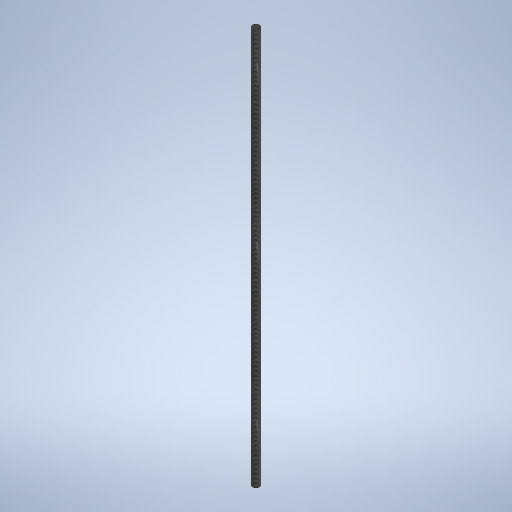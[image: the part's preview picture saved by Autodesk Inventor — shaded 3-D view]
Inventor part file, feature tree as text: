
AUTODESK INVENTOR PART (.ipt)
format: ipt  version: 2024 (Build 280153000, 153)  size: 253,440 bytes
history: native  units: mm
features: extrude x1, thread x1, sketch x1
ambient origin geometry x8: Origin, YZ Plane, XZ Plane, XY Plane, X Axis, Y Axis, Z Axis, Center Point
bodies: Solid1 (feature_tree)
feature tree (3):
  extrude  "Extrusion1"  Depth=450.0mm
  thread  "Thread1"  [1 undecoded]
  sketch  "Sketch1"  dims[d0=450.0mm d1=0.0mm d2=8.0mm d3=450.0mm d4=0.0mm]
note: 1 required parameter value undecoded (feature->parameter linkage not recoverable at this tier; creation-order binding heuristic only, values carry confidence <= 0.55)
